# Revit family: GP Heizkörperregulierventil Eck 5524
name_source: partatom
category: Rohrzubehör
units: mm (PartAtom-declared; Revit-internal decimal feet)

## family parameters
Arbeitsebenenbasiert = Nein
Beim Laden mit Abzugskörper schneiden = Nein
Bemaßung runder Anschluss = Durchmesser verwenden
Gemeinsam genutzt = Nein
Immer vertikal = Ja
OmniClass-Nummer = 23.65.55.14
OmniClass-Titel = Valves for Liquid Services
Teiletyp = Unterbricht

## types (1)
- GP Heizkörperregulierventil Eck 5524
    Ausführungen = Universalmodelle mit Spezialmuffen für Gewinderohr und Klemmsetanschluss, vernickelt.
    Gehäuse = vernickeltes Messing
    Handrad = Kunststoff, weiß
    Hersteller = HERZ Armaturen Ges.m.b.H.
    Max.Betriebsdruck = 1000000.0 Pa
    Max.Betriebstemperatur = 120 °C
    Medium = Heizwasserqualität entsprechend ÖNORM H 5195 bzw. VDI-Richtllinie 2035.
    R01 = 10.5 mm  [stored 0.0344488 ft]
    S01 = 10 mm  [stored 0.0328084 ft]
    S04 = 45 mm  [stored 0.147638 ft]
    SCRNCODE = 05;00;02
    SCRNSEQ = ARM;ARM_TYP="ALLF";2
    URL = www.herz-armaturen.at

note: [stored X ft] marks values corroborated as IEEE doubles in the binary element streams (Revit-internal decimal feet)
